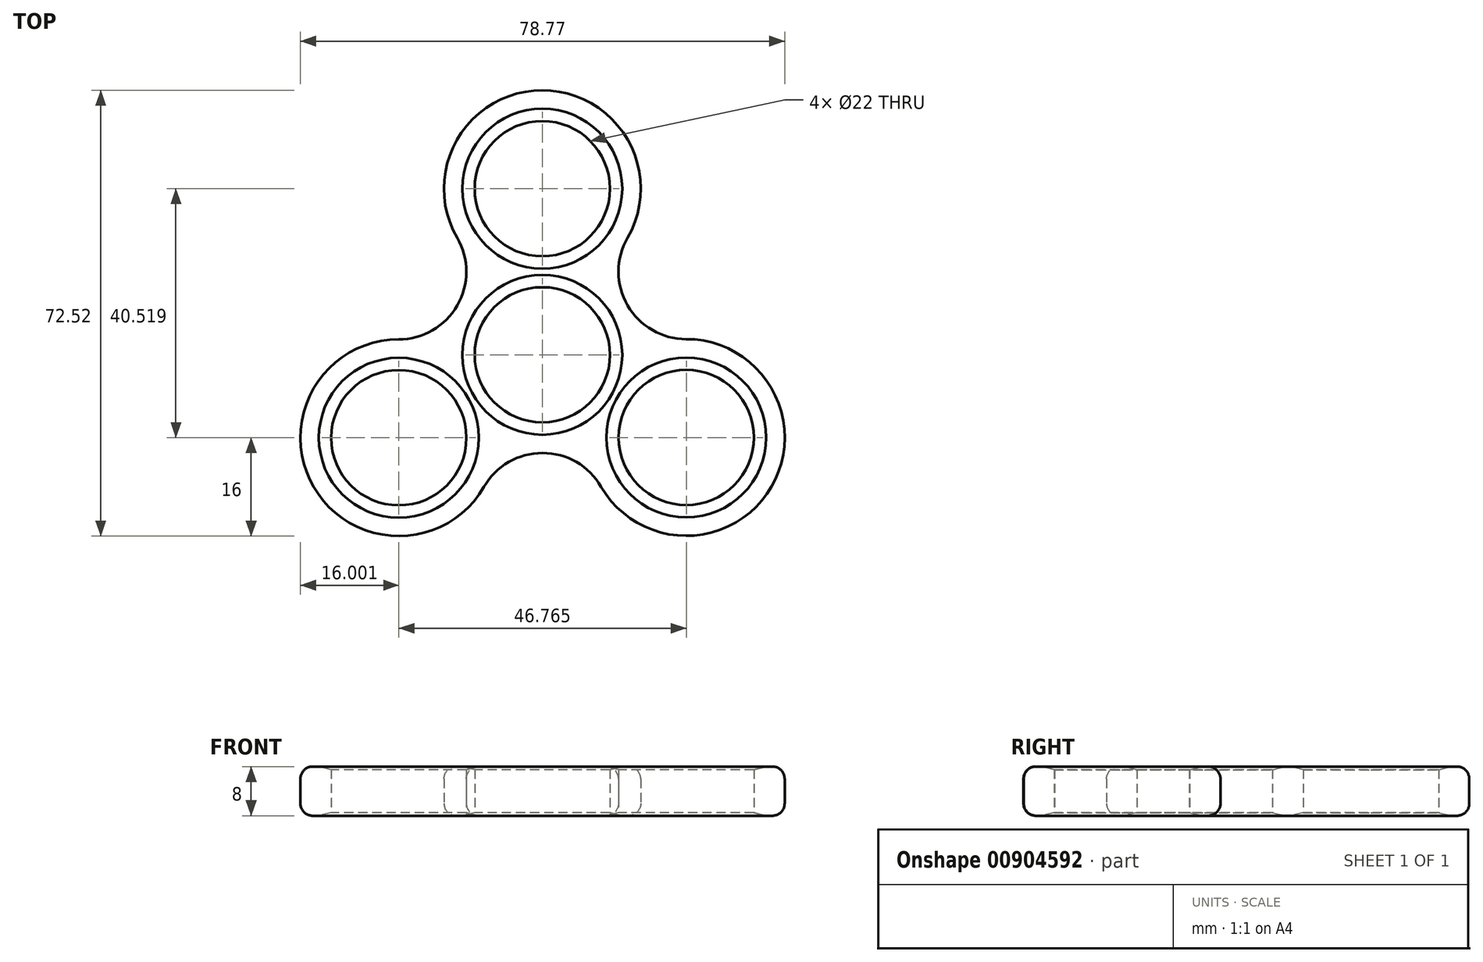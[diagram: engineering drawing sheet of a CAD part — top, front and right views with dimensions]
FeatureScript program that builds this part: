
annotation { "Feature Type Name" : "Feature", "Feature Type Description" : "" }
export const myFeature = defineFeature(function(context is Context, id is Id, definition is map)
    precondition{}
    {
        {
            var Q0;
            Q0=qCreatedBy(makeId("Top.planeOp"),FACE);
            var sketch = newSketch(context, id + "F0", { "sketchPlane" : qUnion([Q0])});
            skCircle(sketch, "E0", {"center": v(0, 0) * mm, "radius": 27.04 * mm});
            skCircle(sketch, "E1", {"center": v(0, 27.04) * mm, "radius": 11 * mm});
            skCircle(sketch, "E2.1.0", {"center": v(-23.37, 13.52) * mm, "radius": 11 * mm});
            skCircle(sketch, "E2.2.0", {"center": v(-23.35, -13.48) * mm, "radius": 11 * mm});
            skCircle(sketch, "E2.3.0", {"center": v(0.04, -26.96) * mm, "radius": 11 * mm});
            skCircle(sketch, "E2.4.0", {"center": v(23.42, -13.44) * mm, "radius": 11 * mm});
            skCircle(sketch, "E2.5.0", {"center": v(23.4, 13.56) * mm, "radius": 11 * mm});
            skPoint(sketch, "E2.center", {"position": v(0.02, 0.04) * mm});
            skCircle(sketch, "E3", {"center": v(0, 27.04) * mm, "radius": 16 * mm});
            skCircle(sketch, "E4.1.0", {"center": v(-23.35, -13.48) * mm, "radius": 16 * mm});
            skCircle(sketch, "E4.2.0", {"center": v(23.42, -13.44) * mm, "radius": 16 * mm});
            skCircle(sketch, "E5", {"center": v(0, 0) * mm, "radius": 11 * mm});
            skSolve(sketch);
        }
        {
            var Q0;
            {var subQ0=sQuery(id+"F0.wireOp",EDGE,"E3");var subQ1=sQuery(id+"F0.wireOp",EDGE,"E0");var subQ2=makeQuery(id+"F0.imprint","INTERSECT",VERTEX,{"disambiguationData":[OD(0.0)],"derivedFrom":[subQ1,subQ0]});Q0=makeQuery(id+"F0.imprint","IMPRINT",FACE,{"disambiguationData":[TD([[makeQuery(id+"F0.imprint","IMPRINT",EDGE,{"disambiguationData":[TD([[subQ2,-1.0]])],"derivedFrom":subQ1}),-1.0]])]});}
            var Q1;
            {var subQ0=sQuery(id+"F0.wireOp",EDGE,"E3");var subQ1=sQuery(id+"F0.wireOp",EDGE,"E0");var subQ2=makeQuery(id+"F0.imprint","INTERSECT",VERTEX,{"disambiguationData":[OD(0.0)],"derivedFrom":[subQ1,subQ0]});Q1=makeQuery(id+"F0.imprint","IMPRINT",FACE,{"disambiguationData":[TD([[makeQuery(id+"F0.imprint","IMPRINT",EDGE,{"disambiguationData":[TD([[subQ2,-1.0]])],"derivedFrom":subQ1}),1.0]])]});}
            var Q2;
            {var subQ0=sQuery(id+"F0.wireOp",EDGE,"E4.2.0");var subQ1=sQuery(id+"F0.wireOp",EDGE,"E0");var subQ2=makeQuery(id+"F0.imprint","INTERSECT",VERTEX,{"disambiguationData":[OD(1.0)],"derivedFrom":[subQ1,subQ0]});Q2=makeQuery(id+"F0.imprint","IMPRINT",FACE,{"disambiguationData":[TD([[makeQuery(id+"F0.imprint","IMPRINT",EDGE,{"disambiguationData":[TD([[subQ2,-1.0]])],"derivedFrom":subQ1}),-1.0]])]});}
            var Q3;
            {var subQ0=sQuery(id+"F0.wireOp",EDGE,"E4.2.0");var subQ1=sQuery(id+"F0.wireOp",EDGE,"E0");var subQ7=makeQuery(id+"F0.imprint","INTERSECT",VERTEX,{"disambiguationData":[OD(1.0)],"derivedFrom":[subQ1,subQ0]});Q3=makeQuery(id+"F0.imprint","IMPRINT",FACE,{"disambiguationData":[TD([[makeQuery(id+"F0.imprint","IMPRINT",EDGE,{"disambiguationData":[TD([[subQ7,-1.0]])],"derivedFrom":subQ1}),1.0]])]});}
            var Q4;
            {var subQ0=sQuery(id+"F0.wireOp",EDGE,"E4.1.0");var subQ1=sQuery(id+"F0.wireOp",EDGE,"E0");var subQ7=makeQuery(id+"F0.imprint","INTERSECT",VERTEX,{"disambiguationData":[OD(0.0)],"derivedFrom":[subQ1,subQ0]});Q4=makeQuery(id+"F0.imprint","IMPRINT",FACE,{"disambiguationData":[TD([[makeQuery(id+"F0.imprint","IMPRINT",EDGE,{"disambiguationData":[TD([[subQ7,-1.0]])],"derivedFrom":subQ1}),1.0]])]});}
            var Q5;
            {var subQ0=sQuery(id+"F0.wireOp",EDGE,"E4.1.0");var subQ1=sQuery(id+"F0.wireOp",EDGE,"E0");var subQ2=makeQuery(id+"F0.imprint","INTERSECT",VERTEX,{"disambiguationData":[OD(0.0)],"derivedFrom":[subQ1,subQ0]});Q5=makeQuery(id+"F0.imprint","IMPRINT",FACE,{"disambiguationData":[TD([[makeQuery(id+"F0.imprint","IMPRINT",EDGE,{"disambiguationData":[TD([[subQ2,-1.0]])],"derivedFrom":subQ1}),-1.0]])]});}
            var Q6;
            {var subQ16=sQuery(id+"F0.wireOp",EDGE,"E5");Q6=makeQuery(id+"F0.imprint","IMPRINT",FACE,{"disambiguationData":[TD([[makeQuery(id+"F0.imprint","IMPRINT",EDGE,{"derivedFrom":subQ16}),-1.0]])]});}
            var Q7;
            {var subQ1=sQuery(id+"F0.wireOp",EDGE,"E2.1.0");var subQ5=sQuery(id+"F0.wireOp",EDGE,"E4.1.0");var subQ6=makeQuery(id+"F0.imprint","INTERSECT",VERTEX,{"derivedFrom":[subQ1,subQ5]});Q7=makeQuery(id+"F0.imprint","IMPRINT",FACE,{"disambiguationData":[TD([[makeQuery(id+"F0.imprint","IMPRINT",EDGE,{"disambiguationData":[TD([[subQ6,-1.0]])],"derivedFrom":subQ1}),-1.0]])]});}
            extrude(context, id + "F1", {"entities" : qUnion([Q0, Q1, Q2, Q3, Q4, Q5, Q6, Q7]), "depth" : 8 * mm, "offsetDistance" : 25 * mm});
        }
        {
            var Q0;
            Q0=makeQuery(id+"F1.opExtrude","CAP_EDGE",EDGE,{"disambiguationData":[OSD([sQuery(id+"F0.wireOp",EDGE,"E2.1.0")])],"isStart":true});
            var Q1;
            Q1=makeQuery(id+"F1.opExtrude","CAP_EDGE",EDGE,{"disambiguationData":[OSD([sQuery(id+"F0.wireOp",EDGE,"E4.1.0")])],"isStart":false});
            fillet(context, id + "F2", {"entities" : qUnion([Q0, Q1]), "radius" : 2 * mm, "tangentPropagation" : true, "allowEdgeOverflow" : false});
        }
        {
            var Q0;
            Q0=makeQuery(id+"F1.opExtrude","CAP_EDGE",EDGE,{"disambiguationData":[OSD([sQuery(id+"F0.wireOp",EDGE,"E5")])],"isStart":true});
            var Q1;
            Q1=makeQuery(id+"F1.opExtrude","CAP_EDGE",EDGE,{"disambiguationData":[OSD([sQuery(id+"F0.wireOp",EDGE,"E2.4.0")])],"isStart":true});
            var Q2;
            Q2=makeQuery(id+"F1.opExtrude","CAP_EDGE",EDGE,{"disambiguationData":[OSD([sQuery(id+"F0.wireOp",EDGE,"E2.2.0")])],"isStart":true});
            var Q3;
            Q3=makeQuery(id+"F1.opExtrude","CAP_EDGE",EDGE,{"disambiguationData":[OSD([sQuery(id+"F0.wireOp",EDGE,"E1")])],"isStart":true});
            chamfer(context, id + "F3", {"entities" : qUnion([Q0, Q1, Q2, Q3]), "chamferType" : ChamferType.TWO_OFFSETS, "width1" : 2 * mm, "oppositeDirection" : false, "width2" : .5 * mm, "tangentPropagation" : true});
        }
        {
            var Q0;
            Q0=makeQuery(id+"F1.opExtrude","CAP_EDGE",EDGE,{"disambiguationData":[OSD([sQuery(id+"F0.wireOp",EDGE,"E1")])],"isStart":false});
            var Q1;
            Q1=makeQuery(id+"F1.opExtrude","CAP_EDGE",EDGE,{"disambiguationData":[OSD([sQuery(id+"F0.wireOp",EDGE,"E5")])],"isStart":false});
            var Q2;
            Q2=makeQuery(id+"F1.opExtrude","CAP_EDGE",EDGE,{"disambiguationData":[OSD([sQuery(id+"F0.wireOp",EDGE,"E2.2.0")])],"isStart":false});
            var Q3;
            Q3=makeQuery(id+"F1.opExtrude","CAP_EDGE",EDGE,{"disambiguationData":[OSD([sQuery(id+"F0.wireOp",EDGE,"E2.4.0")])],"isStart":false});
            chamfer(context, id + "F4", {"entities" : qUnion([Q0, Q1, Q2, Q3]), "chamferType" : ChamferType.TWO_OFFSETS, "width1" : .5 * mm, "oppositeDirection" : false, "width2" : 2 * mm, "tangentPropagation" : true});
        }
    });
